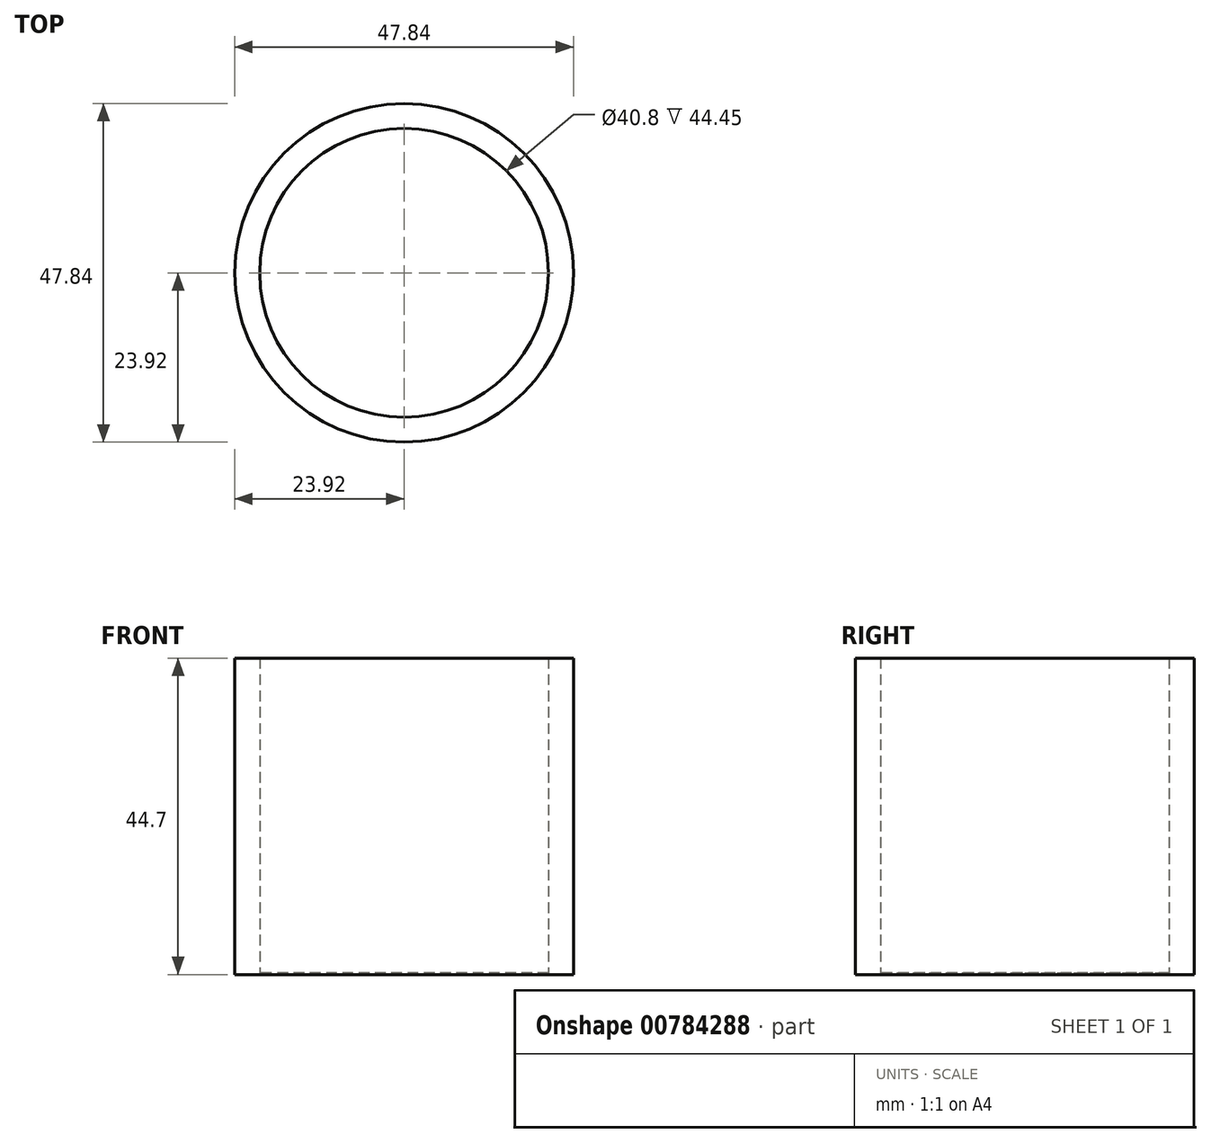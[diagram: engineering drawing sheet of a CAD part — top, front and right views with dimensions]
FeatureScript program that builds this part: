
annotation { "Feature Type Name" : "Feature", "Feature Type Description" : "" }
export const myFeature = defineFeature(function(context is Context, id is Id, definition is map)
    precondition{}
    {
        {
            var Q0;
            Q0=qCreatedBy(makeId("Top.planeOp"),FACE);
            var sketch = newSketch(context, id + "F0", { "sketchPlane" : qUnion([Q0])});
            skCircle(sketch, "E0", {"center": v(0, 0) * mm, "radius": 23.92 * mm});
            skCircle(sketch, "E1", {"center": v(0, 0) * mm, "radius": 20.4 * mm});
            skSolve(sketch);
        }
        {
            var Q0;
            Q0=makeQuery(id+"F0.imprint","IMPRINT",FACE,{"disambiguationData":[TD([[makeQuery(id+"F0.imprint","IMPRINT",EDGE,{"derivedFrom":sQuery(id+"F0.wireOp",EDGE,"E0")}),1.0]])]});
            extrude(context, id + "F1", {"entities" : qUnion([Q0]), "depth" : 44.7 * mm, "offsetDistance" : 25.4 * mm});
        }
        {
            var Q0;
            Q0=makeQuery(id+"F0.imprint","IMPRINT",FACE,{"disambiguationData":[TD([[makeQuery(id+"F0.imprint","IMPRINT",EDGE,{"derivedFrom":sQuery(id+"F0.wireOp",EDGE,"E1")}),1.0]])]});
            extrude(context, id + "F2", {"entities" : qUnion([Q0]), "operationType" : NewBodyOperationType.ADD, "depth" : 0.25 * mm, "offsetDistance" : 25.4 * mm});
        }
        {
            var Q0;
            Q0=qCreatedBy(makeId("Front.planeOp"),FACE);
            var sketch = newSketch(context, id + "F3", { "sketchPlane" : qUnion([Q0])});
            skCircle(sketch, "E2", {"center": v(0, 6.07) * mm, "radius": 4.35 * mm});
            skSolve(sketch);
        }
        {
            var Q0;
            Q0=sQuery(id+"F3.wireOp",EDGE,"E2");
            extrude(context, id + "F4", {"bodyType" : ToolBodyType.SURFACE, "surfaceEntities" : qUnion([Q0]), "depth" : 25.4 * mm, "offsetDistance" : 25.4 * mm});
        }
    });
